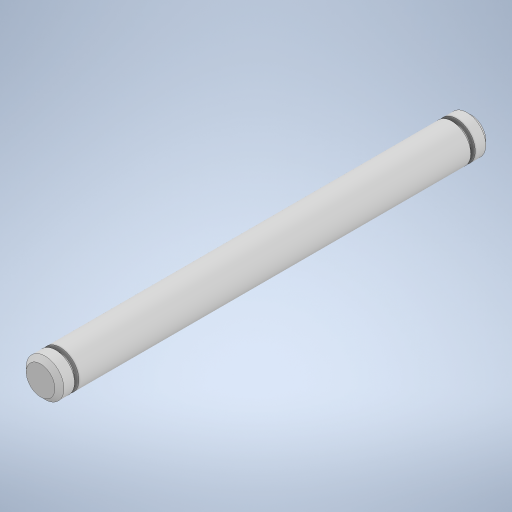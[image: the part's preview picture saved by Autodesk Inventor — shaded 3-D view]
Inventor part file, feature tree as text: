
AUTODESK INVENTOR PART (.ipt)
format: ipt  version: 2024 (Build 280153000, 153)  size: 254,464 bytes
history: native  units: in
note: dims shown in document units (in); Inventor stores cm internally (conversion verified against a paired STEP export)
features: extrude x3, sketch x3, chamfer x1, mirror x1
ambient origin geometry x8: Origin, YZ Plane, XZ Plane, XY Plane, X Axis, Y Axis, Z Axis, Center Point
bodies: Solid1 (feature_tree)
feature tree (8):
  extrude  "Extrusion1"  Depth=1.2998in TaperAngle=0.0deg
  extrude  "Extrusion2"  Depth=0.015in TaperAngle=0.0deg
  extrude  "Extrusion3"  Depth=0.05in TaperAngle=0.0deg
  chamfer  "Chamfer1"  Distance=0.015in Angle=45.0deg
  mirror  "Mirror1"
  sketch  "Sketch1"  dims[d0=0.125in d1=1.2998in d2=0.0in]
  sketch  "Sketch2"  dims[d3=0.0938in d4=0.015in d5=0.0in]
  sketch  "Sketch3"  dims[d6=0.125in d7=0.05in d8=0.0in d9=0.015in d10=0.125in d11=45.0deg]
